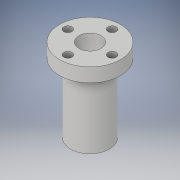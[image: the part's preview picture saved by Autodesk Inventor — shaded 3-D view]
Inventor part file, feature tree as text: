
AUTODESK INVENTOR PART (.ipt)
format: ipt  version: 2019 (Build 230136000, 136)  size: 136,704 bytes
history: native  units: in
note: dims shown in document units (in); Inventor stores cm internally (conversion verified against a paired STEP export)
features: sketch x2, other x2, revolve x1, extrude x1, plane x1
ambient origin geometry x8: Origin, YZ Plane, XZ Plane, XY Plane, X Axis, Y Axis, Z Axis, Center Point
bodies: Solid1 (feature_tree)
feature tree (7):
  revolve  "Revolution1"  [1 undecoded]
  extrude  "Extrusion1"  Depth=0.1575in
  plane  "Work Plane1"
  sketch  "Sketch1"  dims[d1=0.1575in d2=0.4331in]
  sketch  "Sketch2"  dims[d3=0.1969in d4=0.1575in d5=0.9843in d6=90.0deg d7=0.315in d8=0.1181in d9=1.5748in d11=360.0deg d13=1.0in d14=0.0in]
  other  "Work Axis1"
  other  "Work Axis2"
note: 1 required parameter value undecoded (feature->parameter linkage not recoverable at this tier; creation-order binding heuristic only, values carry confidence <= 0.55)
